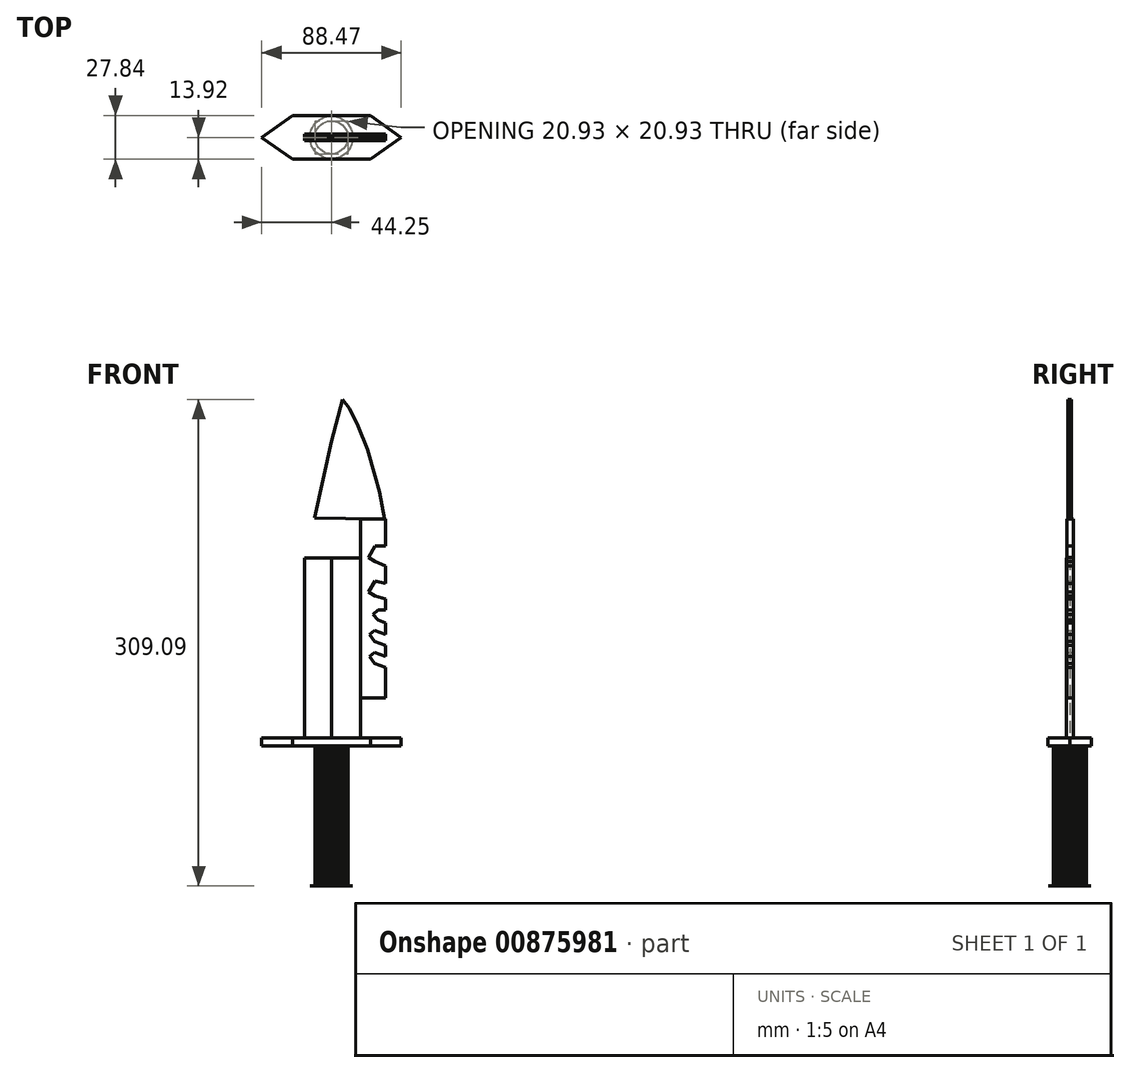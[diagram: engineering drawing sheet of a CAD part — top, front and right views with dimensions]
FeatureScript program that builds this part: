
annotation { "Feature Type Name" : "Feature", "Feature Type Description" : "" }
export const myFeature = defineFeature(function(context is Context, id is Id, definition is map)
    precondition{}
    {
        {
            var Q0;
            Q0=qCreatedBy(makeId("Top.planeOp"),FACE);
            var sketch = newSketch(context, id + "F0", { "sketchPlane" : qUnion([Q0])});
            skCircle(sketch, "E0.cCircle", {"center": v(0, 0) * mm, "radius": 13.55 * mm, "construction": true});
            skLineSegment(sketch, "E0.0", {"start": v(9, -10.17) * mm, "end": v(7.65, -11.22) * mm});
            skLineSegment(sketch, "E0.1", {"start": v(7.65, -11.22) * mm, "end": v(6.18, -12.09) * mm});
            skLineSegment(sketch, "E0.2", {"start": v(6.18, -12.09) * mm, "end": v(4.62, -12.77) * mm});
            skLineSegment(sketch, "E0.3", {"start": v(4.62, -12.77) * mm, "end": v(2.98, -13.25) * mm});
            skLineSegment(sketch, "E0.4", {"start": v(2.98, -13.25) * mm, "end": v(1.3, -13.51) * mm});
            skLineSegment(sketch, "E0.5", {"start": v(1.3, -13.51) * mm, "end": v(-0.4, -13.57) * mm});
            skLineSegment(sketch, "E0.6", {"start": v(-0.4, -13.57) * mm, "end": v(-2.1, -13.41) * mm});
            skLineSegment(sketch, "E0.7", {"start": v(-2.1, -13.41) * mm, "end": v(-3.77, -13.04) * mm});
            skLineSegment(sketch, "E0.8", {"start": v(-3.77, -13.04) * mm, "end": v(-5.38, -12.47) * mm});
            skLineSegment(sketch, "E0.9", {"start": v(-5.38, -12.47) * mm, "end": v(-6.9, -11.7) * mm});
            skLineSegment(sketch, "E0.10", {"start": v(-6.9, -11.7) * mm, "end": v(-8.3, -10.74) * mm});
            skLineSegment(sketch, "E0.11", {"start": v(-8.3, -10.74) * mm, "end": v(-9.59, -9.61) * mm});
            skLineSegment(sketch, "E0.12", {"start": v(-9.59, -9.61) * mm, "end": v(-10.72, -8.33) * mm});
            skLineSegment(sketch, "E0.13", {"start": v(-10.72, -8.33) * mm, "end": v(-11.68, -6.93) * mm});
            skLineSegment(sketch, "E0.14", {"start": v(-11.68, -6.93) * mm, "end": v(-12.45, -5.4) * mm});
            skLineSegment(sketch, "E0.15", {"start": v(-12.45, -5.4) * mm, "end": v(-13.03, -3.8) * mm});
            skLineSegment(sketch, "E0.16", {"start": v(-13.03, -3.8) * mm, "end": v(-13.4, -2.14) * mm});
            skLineSegment(sketch, "E0.17", {"start": v(-13.4, -2.14) * mm, "end": v(-13.57, -0.44) * mm});
            skLineSegment(sketch, "E0.18", {"start": v(-13.57, -0.44) * mm, "end": v(-13.52, 1.26) * mm});
            skLineSegment(sketch, "E0.19", {"start": v(-13.52, 1.26) * mm, "end": v(-13.25, 2.94) * mm});
            skLineSegment(sketch, "E0.20", {"start": v(-13.25, 2.94) * mm, "end": v(-12.78, 4.58) * mm});
            skLineSegment(sketch, "E0.21", {"start": v(-12.78, 4.58) * mm, "end": v(-12.1, 6.15) * mm});
            skLineSegment(sketch, "E0.22", {"start": v(-12.1, 6.15) * mm, "end": v(-11.24, 7.62) * mm});
            skLineSegment(sketch, "E0.23", {"start": v(-11.24, 7.62) * mm, "end": v(-10.2, 8.97) * mm});
            skLineSegment(sketch, "E0.24", {"start": v(-10.2, 8.97) * mm, "end": v(-9, 10.17) * mm});
            skLineSegment(sketch, "E0.25", {"start": v(-9, 10.17) * mm, "end": v(-7.65, 11.22) * mm});
            skLineSegment(sketch, "E0.26", {"start": v(-7.65, 11.22) * mm, "end": v(-6.18, 12.09) * mm});
            skLineSegment(sketch, "E0.27", {"start": v(-6.18, 12.09) * mm, "end": v(-4.62, 12.77) * mm});
            skLineSegment(sketch, "E0.28", {"start": v(-4.62, 12.77) * mm, "end": v(-2.98, 13.25) * mm});
            skLineSegment(sketch, "E0.29", {"start": v(-2.98, 13.25) * mm, "end": v(-1.3, 13.51) * mm});
            skLineSegment(sketch, "E0.30", {"start": v(-1.3, 13.51) * mm, "end": v(0.4, 13.57) * mm});
            skLineSegment(sketch, "E0.31", {"start": v(0.4, 13.57) * mm, "end": v(2.1, 13.41) * mm});
            skLineSegment(sketch, "E0.32", {"start": v(2.1, 13.41) * mm, "end": v(3.77, 13.04) * mm});
            skLineSegment(sketch, "E0.33", {"start": v(3.77, 13.04) * mm, "end": v(5.38, 12.47) * mm});
            skLineSegment(sketch, "E0.34", {"start": v(5.38, 12.47) * mm, "end": v(6.9, 11.7) * mm});
            skLineSegment(sketch, "E0.35", {"start": v(6.9, 11.7) * mm, "end": v(8.3, 10.74) * mm});
            skLineSegment(sketch, "E0.36", {"start": v(8.3, 10.74) * mm, "end": v(9.59, 9.61) * mm});
            skLineSegment(sketch, "E0.37", {"start": v(9.59, 9.61) * mm, "end": v(10.72, 8.33) * mm});
            skLineSegment(sketch, "E0.38", {"start": v(10.72, 8.33) * mm, "end": v(11.68, 6.93) * mm});
            skLineSegment(sketch, "E0.39", {"start": v(11.68, 6.93) * mm, "end": v(12.45, 5.4) * mm});
            skLineSegment(sketch, "E0.40", {"start": v(12.45, 5.4) * mm, "end": v(13.03, 3.8) * mm});
            skLineSegment(sketch, "E0.41", {"start": v(13.03, 3.8) * mm, "end": v(13.4, 2.14) * mm});
            skLineSegment(sketch, "E0.42", {"start": v(13.4, 2.14) * mm, "end": v(13.57, 0.44) * mm});
            skLineSegment(sketch, "E0.43", {"start": v(13.57, 0.44) * mm, "end": v(13.52, -1.26) * mm});
            skLineSegment(sketch, "E0.44", {"start": v(13.52, -1.26) * mm, "end": v(13.25, -2.94) * mm});
            skLineSegment(sketch, "E0.45", {"start": v(13.25, -2.94) * mm, "end": v(12.78, -4.58) * mm});
            skLineSegment(sketch, "E0.46", {"start": v(12.78, -4.58) * mm, "end": v(12.1, -6.15) * mm});
            skLineSegment(sketch, "E0.47", {"start": v(12.1, -6.15) * mm, "end": v(11.24, -7.62) * mm});
            skLineSegment(sketch, "E0.48", {"start": v(11.24, -7.62) * mm, "end": v(10.2, -8.97) * mm});
            skLineSegment(sketch, "E0.49", {"start": v(10.2, -8.97) * mm, "end": v(9, -10.17) * mm});
            skPoint(sketch, "E0.0.midPoint", {"position": v(8.32, -10.7) * mm});
            skSolve(sketch);
        }
        {
            var Q0;
            Q0 = qSketchRegion(id + "F0", true);
            extrude(context, id + "F1", {"entities" : qUnion([Q0]), "depth" : 1 / 50.8 * mm, "offsetDistance" : 25.4 * mm});
        }
        {
            var Q0;
            Q0=makeQuery(id+"F1.opExtrude","CAP_FACE",FACE,{"disambiguationData":[OSD([sQuery(id+"F0.wireOp",EDGE,"E0.0"),sQuery(id+"F0.wireOp",EDGE,"E0.1"),sQuery(id+"F0.wireOp",EDGE,"E0.2"),sQuery(id+"F0.wireOp",EDGE,"E0.3"),sQuery(id+"F0.wireOp",EDGE,"E0.4"),sQuery(id+"F0.wireOp",EDGE,"E0.5"),sQuery(id+"F0.wireOp",EDGE,"E0.6"),sQuery(id+"F0.wireOp",EDGE,"E0.7"),sQuery(id+"F0.wireOp",EDGE,"E0.8"),sQuery(id+"F0.wireOp",EDGE,"E0.9"),sQuery(id+"F0.wireOp",EDGE,"E0.10"),sQuery(id+"F0.wireOp",EDGE,"E0.11"),sQuery(id+"F0.wireOp",EDGE,"E0.12"),sQuery(id+"F0.wireOp",EDGE,"E0.13"),sQuery(id+"F0.wireOp",EDGE,"E0.14"),sQuery(id+"F0.wireOp",EDGE,"E0.15"),sQuery(id+"F0.wireOp",EDGE,"E0.16"),sQuery(id+"F0.wireOp",EDGE,"E0.17"),sQuery(id+"F0.wireOp",EDGE,"E0.18"),sQuery(id+"F0.wireOp",EDGE,"E0.19"),sQuery(id+"F0.wireOp",EDGE,"E0.20"),sQuery(id+"F0.wireOp",EDGE,"E0.21"),sQuery(id+"F0.wireOp",EDGE,"E0.22"),sQuery(id+"F0.wireOp",EDGE,"E0.23"),sQuery(id+"F0.wireOp",EDGE,"E0.24"),sQuery(id+"F0.wireOp",EDGE,"E0.25"),sQuery(id+"F0.wireOp",EDGE,"E0.26"),sQuery(id+"F0.wireOp",EDGE,"E0.27"),sQuery(id+"F0.wireOp",EDGE,"E0.28"),sQuery(id+"F0.wireOp",EDGE,"E0.29"),sQuery(id+"F0.wireOp",EDGE,"E0.30"),sQuery(id+"F0.wireOp",EDGE,"E0.31"),sQuery(id+"F0.wireOp",EDGE,"E0.32"),sQuery(id+"F0.wireOp",EDGE,"E0.33"),sQuery(id+"F0.wireOp",EDGE,"E0.34"),sQuery(id+"F0.wireOp",EDGE,"E0.35"),sQuery(id+"F0.wireOp",EDGE,"E0.36"),sQuery(id+"F0.wireOp",EDGE,"E0.37"),sQuery(id+"F0.wireOp",EDGE,"E0.38"),sQuery(id+"F0.wireOp",EDGE,"E0.39"),sQuery(id+"F0.wireOp",EDGE,"E0.40"),sQuery(id+"F0.wireOp",EDGE,"E0.41"),sQuery(id+"F0.wireOp",EDGE,"E0.42"),sQuery(id+"F0.wireOp",EDGE,"E0.43"),sQuery(id+"F0.wireOp",EDGE,"E0.44"),sQuery(id+"F0.wireOp",EDGE,"E0.45"),sQuery(id+"F0.wireOp",EDGE,"E0.46"),sQuery(id+"F0.wireOp",EDGE,"E0.47"),sQuery(id+"F0.wireOp",EDGE,"E0.48"),sQuery(id+"F0.wireOp",EDGE,"E0.49")])],"isStart":false});
            var sketch = newSketch(context, id + "F2", { "sketchPlane" : qUnion([Q0])});
            skCircle(sketch, "E1.cCircle", {"center": v(0, 0) * mm, "radius": 10.45 * mm, "construction": true});
            skLineSegment(sketch, "E1.0", {"start": v(3.77, -9.78) * mm, "end": v(2.2, -10.25) * mm});
            skLineSegment(sketch, "E1.1", {"start": v(2.2, -10.25) * mm, "end": v(0.56, -10.47) * mm});
            skLineSegment(sketch, "E1.2", {"start": v(0.56, -10.47) * mm, "end": v(-1.08, -10.42) * mm});
            skLineSegment(sketch, "E1.3", {"start": v(-1.08, -10.42) * mm, "end": v(-2.7, -10.13) * mm});
            skLineSegment(sketch, "E1.4", {"start": v(-2.7, -10.13) * mm, "end": v(-4.25, -9.58) * mm});
            skLineSegment(sketch, "E1.5", {"start": v(-4.25, -9.58) * mm, "end": v(-5.7, -8.8) * mm});
            skLineSegment(sketch, "E1.6", {"start": v(-5.7, -8.8) * mm, "end": v(-7, -7.8) * mm});
            skLineSegment(sketch, "E1.7", {"start": v(-7, -7.8) * mm, "end": v(-8.14, -6.6) * mm});
            skLineSegment(sketch, "E1.8", {"start": v(-8.14, -6.6) * mm, "end": v(-9.07, -5.25) * mm});
            skLineSegment(sketch, "E1.9", {"start": v(-9.07, -5.25) * mm, "end": v(-9.78, -3.77) * mm});
            skLineSegment(sketch, "E1.10", {"start": v(-9.78, -3.77) * mm, "end": v(-10.25, -2.2) * mm});
            skLineSegment(sketch, "E1.11", {"start": v(-10.25, -2.2) * mm, "end": v(-10.47, -0.56) * mm});
            skLineSegment(sketch, "E1.12", {"start": v(-10.47, -0.56) * mm, "end": v(-10.42, 1.08) * mm});
            skLineSegment(sketch, "E1.13", {"start": v(-10.42, 1.08) * mm, "end": v(-10.13, 2.7) * mm});
            skLineSegment(sketch, "E1.14", {"start": v(-10.13, 2.7) * mm, "end": v(-9.58, 4.25) * mm});
            skLineSegment(sketch, "E1.15", {"start": v(-9.58, 4.25) * mm, "end": v(-8.8, 5.7) * mm});
            skLineSegment(sketch, "E1.16", {"start": v(-8.8, 5.7) * mm, "end": v(-7.8, 7) * mm});
            skLineSegment(sketch, "E1.17", {"start": v(-7.8, 7) * mm, "end": v(-6.6, 8.14) * mm});
            skLineSegment(sketch, "E1.18", {"start": v(-6.6, 8.14) * mm, "end": v(-5.25, 9.07) * mm});
            skLineSegment(sketch, "E1.19", {"start": v(-5.25, 9.07) * mm, "end": v(-3.77, 9.78) * mm});
            skLineSegment(sketch, "E1.20", {"start": v(-3.77, 9.78) * mm, "end": v(-2.2, 10.25) * mm});
            skLineSegment(sketch, "E1.21", {"start": v(-2.2, 10.25) * mm, "end": v(-0.56, 10.47) * mm});
            skLineSegment(sketch, "E1.22", {"start": v(-0.56, 10.47) * mm, "end": v(1.08, 10.42) * mm});
            skLineSegment(sketch, "E1.23", {"start": v(1.08, 10.42) * mm, "end": v(2.7, 10.13) * mm});
            skLineSegment(sketch, "E1.24", {"start": v(2.7, 10.13) * mm, "end": v(4.25, 9.58) * mm});
            skLineSegment(sketch, "E1.25", {"start": v(4.25, 9.58) * mm, "end": v(5.7, 8.8) * mm});
            skLineSegment(sketch, "E1.26", {"start": v(5.7, 8.8) * mm, "end": v(7, 7.8) * mm});
            skLineSegment(sketch, "E1.27", {"start": v(7, 7.8) * mm, "end": v(8.14, 6.6) * mm});
            skLineSegment(sketch, "E1.28", {"start": v(8.14, 6.6) * mm, "end": v(9.07, 5.25) * mm});
            skLineSegment(sketch, "E1.29", {"start": v(9.07, 5.25) * mm, "end": v(9.78, 3.77) * mm});
            skLineSegment(sketch, "E1.30", {"start": v(9.78, 3.77) * mm, "end": v(10.25, 2.2) * mm});
            skLineSegment(sketch, "E1.31", {"start": v(10.25, 2.2) * mm, "end": v(10.47, 0.56) * mm});
            skLineSegment(sketch, "E1.32", {"start": v(10.47, 0.56) * mm, "end": v(10.42, -1.08) * mm});
            skLineSegment(sketch, "E1.33", {"start": v(10.42, -1.08) * mm, "end": v(10.13, -2.7) * mm});
            skLineSegment(sketch, "E1.34", {"start": v(10.13, -2.7) * mm, "end": v(9.58, -4.25) * mm});
            skLineSegment(sketch, "E1.35", {"start": v(9.58, -4.25) * mm, "end": v(8.8, -5.7) * mm});
            skLineSegment(sketch, "E1.36", {"start": v(8.8, -5.7) * mm, "end": v(7.8, -7) * mm});
            skLineSegment(sketch, "E1.37", {"start": v(7.8, -7) * mm, "end": v(6.6, -8.14) * mm});
            skLineSegment(sketch, "E1.38", {"start": v(6.6, -8.14) * mm, "end": v(5.25, -9.07) * mm});
            skLineSegment(sketch, "E1.39", {"start": v(5.25, -9.07) * mm, "end": v(3.77, -9.78) * mm});
            skPoint(sketch, "E1.0.midPoint", {"position": v(2.98, -10.02) * mm});
            skSolve(sketch);
        }
        {
            var Q0;
            Q0 = qSketchRegion(id + "F2", true);
            extrude(context, id + "F3", {"entities" : qUnion([Q0]), "operationType" : NewBodyOperationType.ADD, "depth" : 88.9 * mm, "offsetDistance" : 25.4 * mm});
        }
        {
            var Q0;
            Q0=makeQuery(id+"F3.opExtrude","CAP_FACE",FACE,{"disambiguationData":[OSD([sQuery(id+"F2.wireOp",EDGE,"E1.0"),sQuery(id+"F2.wireOp",EDGE,"E1.1"),sQuery(id+"F2.wireOp",EDGE,"E1.2"),sQuery(id+"F2.wireOp",EDGE,"E1.3"),sQuery(id+"F2.wireOp",EDGE,"E1.4"),sQuery(id+"F2.wireOp",EDGE,"E1.5"),sQuery(id+"F2.wireOp",EDGE,"E1.6"),sQuery(id+"F2.wireOp",EDGE,"E1.7"),sQuery(id+"F2.wireOp",EDGE,"E1.8"),sQuery(id+"F2.wireOp",EDGE,"E1.9"),sQuery(id+"F2.wireOp",EDGE,"E1.10"),sQuery(id+"F2.wireOp",EDGE,"E1.11"),sQuery(id+"F2.wireOp",EDGE,"E1.12"),sQuery(id+"F2.wireOp",EDGE,"E1.13"),sQuery(id+"F2.wireOp",EDGE,"E1.14"),sQuery(id+"F2.wireOp",EDGE,"E1.15"),sQuery(id+"F2.wireOp",EDGE,"E1.16"),sQuery(id+"F2.wireOp",EDGE,"E1.17"),sQuery(id+"F2.wireOp",EDGE,"E1.18"),sQuery(id+"F2.wireOp",EDGE,"E1.19"),sQuery(id+"F2.wireOp",EDGE,"E1.20"),sQuery(id+"F2.wireOp",EDGE,"E1.21"),sQuery(id+"F2.wireOp",EDGE,"E1.22"),sQuery(id+"F2.wireOp",EDGE,"E1.23"),sQuery(id+"F2.wireOp",EDGE,"E1.24"),sQuery(id+"F2.wireOp",EDGE,"E1.25"),sQuery(id+"F2.wireOp",EDGE,"E1.26"),sQuery(id+"F2.wireOp",EDGE,"E1.27"),sQuery(id+"F2.wireOp",EDGE,"E1.28"),sQuery(id+"F2.wireOp",EDGE,"E1.29"),sQuery(id+"F2.wireOp",EDGE,"E1.30"),sQuery(id+"F2.wireOp",EDGE,"E1.31"),sQuery(id+"F2.wireOp",EDGE,"E1.32"),sQuery(id+"F2.wireOp",EDGE,"E1.33"),sQuery(id+"F2.wireOp",EDGE,"E1.34"),sQuery(id+"F2.wireOp",EDGE,"E1.35"),sQuery(id+"F2.wireOp",EDGE,"E1.36"),sQuery(id+"F2.wireOp",EDGE,"E1.37"),sQuery(id+"F2.wireOp",EDGE,"E1.38"),sQuery(id+"F2.wireOp",EDGE,"E1.39")])],"isStart":false});
            var sketch = newSketch(context, id + "F4", { "sketchPlane" : qUnion([Q0])});
            skLineSegment(sketch, "E2.bottom", {"start": v(24.8, -13.92) * mm, "end": v(-24.8, -13.92) * mm});
            skLineSegment(sketch, "E2.top", {"start": v(24.8, 13.92) * mm, "end": v(-24.8, 13.92) * mm});
            skLineSegment(sketch, "E2.left", {"start": v(24.8, -13.92) * mm, "end": v(24.8, 13.92) * mm});
            skLineSegment(sketch, "E2.right", {"start": v(-24.8, -13.92) * mm, "end": v(-24.8, 13.92) * mm});
            skPoint(sketch, "E2.middle", {"position": v(0, 0) * mm});
            skSolve(sketch);
        }
        {
            var Q0;
            Q0 = qSketchRegion(id + "F4", true);
            extrude(context, id + "F5", {"entities" : qUnion([Q0]), "operationType" : NewBodyOperationType.ADD, "depth" : 5.08 * mm, "offsetDistance" : 25.4 * mm});
        }
        {
            var Q0;
            Q0=makeQuery(id+"F5.opExtrude","CAP_FACE",FACE,{"disambiguationData":[OSD([sQuery(id+"F4.wireOp",EDGE,"E2.bottom"),sQuery(id+"F4.wireOp",EDGE,"E2.top"),sQuery(id+"F4.wireOp",EDGE,"E2.left"),sQuery(id+"F4.wireOp",EDGE,"E2.right")])],"isStart":true});
            var sketch = newSketch(context, id + "F6", { "sketchPlane" : qUnion([Q0])});
            skLineSegment(sketch, "E3", {"start": v(-24.8, -13.92) * mm, "end": v(-44.25, 0) * mm});
            skLineSegment(sketch, "E4", {"start": v(-44.25, 0) * mm, "end": v(-24.8, 13.92) * mm});
            skLineSegment(sketch, "E5", {"start": v(24.8, 13.92) * mm, "end": v(44.22, 0) * mm});
            skLineSegment(sketch, "E6", {"start": v(44.22, 0) * mm, "end": v(24.8, -13.92) * mm});
            skSolve(sketch);
        }
        {
            var Q0;
            Q0=makeQuery(id+"F6.imprint","IMPRINT",FACE,{"disambiguationData":[TD([[makeQuery(id+"F6.imprint","IMPRINT",EDGE,{"derivedFrom":sQuery(id+"F6.wireOp",EDGE,"E3")}),-1.0]])]});
            extrude(context, id + "F7", {"entities" : qUnion([Q0]), "operationType" : NewBodyOperationType.ADD, "oppositeDirection" : true, "depth" : 5.08 * mm, "offsetDistance" : 25.4 * mm});
        }
        {
            var Q0;
            Q0=makeQuery(id+"F6.imprint","IMPRINT",FACE,{"disambiguationData":[TD([[makeQuery(id+"F6.imprint","IMPRINT",EDGE,{"derivedFrom":sQuery(id+"F6.wireOp",EDGE,"E5")}),-1.0]])]});
            extrude(context, id + "F8", {"entities" : qUnion([Q0]), "operationType" : NewBodyOperationType.ADD, "oppositeDirection" : true, "depth" : 5.08 * mm, "offsetDistance" : 25.4 * mm});
        }
        {
            var Q0;
            {var subQ0=sQuery(id+"F4.wireOp",EDGE,"E2.left");var subQ1=sQuery(id+"F4.wireOp",EDGE,"E2.right");Q0=makeQuery(id+"F8.boolean.opBoolean","MERGE",FACE,{"derivedFrom":[makeQuery(id+"F7.boolean.opBoolean","MERGE",FACE,{"derivedFrom":[makeQuery(id+"F5.opExtrude","CAP_FACE",FACE,{"disambiguationData":[OSD([sQuery(id+"F4.wireOp",EDGE,"E2.bottom"),sQuery(id+"F4.wireOp",EDGE,"E2.top"),subQ0,subQ1])],"isStart":false}),makeQuery(id+"F7.opExtrude","CAP_FACE",FACE,{"disambiguationData":[OSD([subQ1,sQuery(id+"F6.wireOp",EDGE,"E3"),sQuery(id+"F6.wireOp",EDGE,"E4")])],"isStart":false})]}),makeQuery(id+"F8.opExtrude","CAP_FACE",FACE,{"disambiguationData":[OSD([subQ0,sQuery(id+"F6.wireOp",EDGE,"E5"),sQuery(id+"F6.wireOp",EDGE,"E6")])],"isStart":false})]});}
            var sketch = newSketch(context, id + "F9", { "sketchPlane" : qUnion([Q0])});
            skPoint(sketch, "E7.firstSnap0", {"position": v(34.5, 6.96) * mm});
            skLineSegment(sketch, "E7.bottom", {"start": v(34.5, 2.26) * mm, "end": v(-17.1, 2.26) * mm});
            skLineSegment(sketch, "E7.top", {"start": v(34.5, -2.17) * mm, "end": v(-17.1, -2.17) * mm});
            skLineSegment(sketch, "E7.left", {"start": v(34.5, 2.26) * mm, "end": v(34.5, -2.17) * mm});
            skLineSegment(sketch, "E7.right", {"start": v(-17.1, 2.26) * mm, "end": v(-17.1, -2.17) * mm});
            skSolve(sketch);
        }
        {
            var Q0;
            Q0 = qSketchRegion(id + "F9", true);
            extrude(context, id + "F10", {"entities" : qUnion([Q0]), "operationType" : NewBodyOperationType.ADD, "depth" : 1 / 50.8 * mm, "offsetDistance" : 25.4 * mm});
        }
        {
            var Q0;
            Q0=makeQuery(id+"F10.opExtrude","CAP_FACE",FACE,{"disambiguationData":[OSD([sQuery(id+"F9.wireOp",EDGE,"E7.bottom"),sQuery(id+"F9.wireOp",EDGE,"E7.top"),sQuery(id+"F9.wireOp",EDGE,"E7.left"),sQuery(id+"F9.wireOp",EDGE,"E7.right")])],"isStart":false});
            var sketch = newSketch(context, id + "F11", { "sketchPlane" : qUnion([Q0])});
            skLineSegment(sketch, "E8.bottom", {"start": v(0, 2.26) * mm, "end": v(18.53, 2.26) * mm});
            skLineSegment(sketch, "E8.top", {"start": v(0, -2.17) * mm, "end": v(18.53, -2.17) * mm});
            skLineSegment(sketch, "E8.left", {"start": v(0, 2.26) * mm, "end": v(0, -2.17) * mm});
            skLineSegment(sketch, "E8.right", {"start": v(18.53, 2.26) * mm, "end": v(18.53, -2.17) * mm});
            skSolve(sketch);
        }
        {
            var Q0;
            Q0 = qSketchRegion(id + "F11", true);
            extrude(context, id + "F12", {"entities" : qUnion([Q0]), "operationType" : NewBodyOperationType.ADD, "depth" : 114.3 * mm, "offsetDistance" : 25.4 * mm});
        }
        {
            var Q0;
            {var subQ0=sQuery(id+"F9.wireOp",EDGE,"E7.right");var subQ1=sQuery(id+"F9.wireOp",EDGE,"E7.top");var subQ2=sQuery(id+"F9.wireOp",EDGE,"E7.bottom");Q0=makeQuery(id+"F12.boolean.opBoolean","SPLIT",FACE,{"disambiguationData":[TD([makeQuery(id+"F10.opExtrude","SWEPT_FACE",FACE,{"disambiguationData":[OSD([subQ0])]})])],"derivedFrom":makeQuery(id+"F10.opExtrude","CAP_FACE",FACE,{"disambiguationData":[OSD([subQ2,subQ1,sQuery(id+"F9.wireOp",EDGE,"E7.left"),subQ0])],"isStart":false})});}
            var sketch = newSketch(context, id + "F13", { "sketchPlane" : qUnion([Q0])});
            skLineSegment(sketch, "E9", {"start": v(0, 2.26) * mm, "end": v(-17.1, 0) * mm});
            skLineSegment(sketch, "E10", {"start": v(-17.1, 0) * mm, "end": v(0, -2.17) * mm});
            skLineSegment(sketch, "E11", {"start": v(0, -2.17) * mm, "end": v(0, 2.26) * mm});
            skSolve(sketch);
        }
        {
            var Q0;
            Q0=makeQuery(id+"F13.imprint","IMPRINT",FACE,{"disambiguationData":[TD([[makeQuery(id+"F13.imprint","IMPRINT",EDGE,{"derivedFrom":sQuery(id+"F13.wireOp",EDGE,"E9")}),1.0]])]});
            extrude(context, id + "F14", {"entities" : qUnion([Q0]), "operationType" : NewBodyOperationType.ADD, "depth" : 114.3 * mm, "offsetDistance" : 25.4 * mm});
        }
        {
            var Q0;
            Q0=makeQuery(id+"F12.boolean.opBoolean","MERGE",FACE,{"derivedFrom":[makeQuery(id+"F10.opExtrude","SWEPT_FACE",FACE,{"disambiguationData":[OSD([sQuery(id+"F9.wireOp",EDGE,"E7.bottom")])]}),makeQuery(id+"F12.opExtrude","SWEPT_FACE",FACE,{"disambiguationData":[OSD([sQuery(id+"F11.wireOp",EDGE,"E8.bottom")])]})]});
            var sketch = newSketch(context, id + "F15", { "sketchPlane" : qUnion([Q0])});
            skLineSegment(sketch, "E12", {"start": v(-34.5, 119.38) * mm, "end": v(-34.5, 124.43) * mm});
            skLineSegment(sketch, "E13", {"start": v(-34.5, 124.43) * mm, "end": v(-23.3, 126.84) * mm});
            skLineSegment(sketch, "E14", {"start": v(-23.26, 126.61) * mm, "end": v(-19.36, 131.77) * mm});
            skLineSegment(sketch, "E15", {"start": v(-19.36, 131.77) * mm, "end": v(-23.41, 134.83) * mm});
            skLineSegment(sketch, "E16", {"start": v(-23.41, 134.83) * mm, "end": v(-34.5, 131.77) * mm});
            skLineSegment(sketch, "E17", {"start": v(-34.5, 131.77) * mm, "end": v(-34.5, 138.87) * mm});
            skLineSegment(sketch, "E18", {"start": v(-34.5, 138.87) * mm, "end": v(-27.46, 141.44) * mm});
            skLineSegment(sketch, "E19", {"start": v(-27.46, 141.44) * mm, "end": v(-24.07, 145.92) * mm});
            skLineSegment(sketch, "E20", {"start": v(-24.07, 145.92) * mm, "end": v(-27.46, 148.49) * mm});
            skLineSegment(sketch, "E21", {"start": v(-27.46, 148.49) * mm, "end": v(-34.5, 145.92) * mm});
            skLineSegment(sketch, "E22", {"start": v(-34.5, 145.92) * mm, "end": v(-34.5, 152.68) * mm});
            skLineSegment(sketch, "E23", {"start": v(-34.5, 152.68) * mm, "end": v(-27.46, 155.25) * mm});
            skLineSegment(sketch, "E24", {"start": v(-27.46, 155.25) * mm, "end": v(-24.07, 159.74) * mm});
            skLineSegment(sketch, "E25", {"start": v(-24.07, 159.74) * mm, "end": v(-27.46, 162.3) * mm});
            skLineSegment(sketch, "E26", {"start": v(-27.46, 162.3) * mm, "end": v(-34.5, 159.74) * mm});
            skLineSegment(sketch, "E27", {"start": v(-34.5, 159.74) * mm, "end": v(-34.5, 167.06) * mm});
            skLineSegment(sketch, "E28", {"start": v(-34.5, 167.06) * mm, "end": v(-29.64, 169.14) * mm});
            skLineSegment(sketch, "E29", {"start": v(-29.64, 169.14) * mm, "end": v(-26.5, 172.52) * mm});
            skLineSegment(sketch, "E30", {"start": v(-26.5, 172.52) * mm, "end": v(-29.64, 175.42) * mm});
            skLineSegment(sketch, "E31", {"start": v(-29.64, 175.42) * mm, "end": v(-34.5, 175.42) * mm});
            skLineSegment(sketch, "E32", {"start": v(-34.5, 175.42) * mm, "end": v(-34.5, 182.4) * mm});
            skLineSegment(sketch, "E33", {"start": v(-34.5, 182.4) * mm, "end": v(-27.86, 184.14) * mm});
            skLineSegment(sketch, "E34", {"start": v(-27.86, 184.14) * mm, "end": v(-23.5, 186.9) * mm});
            skLineSegment(sketch, "E35", {"start": v(-23.5, 186.9) * mm, "end": v(-27.86, 193.8) * mm});
            skLineSegment(sketch, "E36", {"start": v(-27.86, 193.8) * mm, "end": v(-34.5, 192.31) * mm});
            skLineSegment(sketch, "E37", {"start": v(-34.5, 192.31) * mm, "end": v(-34.5, 203.43) * mm});
            skLineSegment(sketch, "E38", {"start": v(-34.5, 203.43) * mm, "end": v(-27.86, 206.05) * mm});
            skLineSegment(sketch, "E39", {"start": v(-27.86, 206.05) * mm, "end": v(-23.5, 208.63) * mm});
            skLineSegment(sketch, "E40", {"start": v(-23.5, 208.63) * mm, "end": v(-27.86, 216.03) * mm});
            skLineSegment(sketch, "E41", {"start": v(-27.86, 216.03) * mm, "end": v(-34.5, 216.03) * mm});
            skLineSegment(sketch, "E42", {"start": v(-34.5, 216.03) * mm, "end": v(-34.5, 233.07) * mm});
            skLineSegment(sketch, "E43", {"start": v(-34.5, 233.07) * mm, "end": v(-18.53, 233.07) * mm});
            skLineSegment(sketch, "E44", {"start": v(-18.53, 233.07) * mm, "end": v(-18.53, 119.38) * mm});
            skLineSegment(sketch, "E45", {"start": v(-18.53, 119.38) * mm, "end": v(-34.5, 119.38) * mm});
            skLineSegment(sketch, "E46.top", {"start": v(-18.53, 233.07) * mm, "end": v(-34.5, 233.07) * mm});
            skLineSegment(sketch, "E46.left", {"start": v(-18.53, 119.38) * mm, "end": v(-18.53, 233.07) * mm});
            skLineSegment(sketch, "E46.right", {"start": v(-34.5, 119.38) * mm, "end": v(-34.5, 233.07) * mm});
            skSolve(sketch);
        }
        {
            var Q0;
            {var subQ8=sQuery(id+"F15.wireOp",EDGE,"E19");Q0=makeQuery(id+"F15.imprint","IMPRINT",FACE,{"disambiguationData":[TD([[makeQuery(id+"F15.imprint","IMPRINT",EDGE,{"derivedFrom":subQ8}),-1.0]])]});}
            extrude(context, id + "F16", {"entities" : qUnion([Q0]), "operationType" : NewBodyOperationType.ADD, "oppositeDirection" : true, "depth" : 4.06 * mm, "offsetDistance" : 25.4 * mm});
        }
        {
            var Q0;
            Q0=qCreatedBy(makeId("Front.planeOp"),FACE);
            var sketch = newSketch(context, id + "F17", { "sketchPlane" : qUnion([Q0])});
            skLineSegment(sketch, "E47", {"start": v(33.72, 233) * mm, "end": v(30.61, 250.21) * mm});
            skLineSegment(sketch, "E48", {"start": v(30.61, 250.21) * mm, "end": v(27.63, 260.38) * mm});
            skLineSegment(sketch, "E49", {"start": v(27.63, 260.38) * mm, "end": v(23.05, 277.19) * mm});
            skLineSegment(sketch, "E50", {"start": v(23.05, 277.19) * mm, "end": v(16.9, 292.23) * mm});
            skLineSegment(sketch, "E51", {"start": v(16.9, 292.23) * mm, "end": v(11.68, 303.23) * mm});
            skLineSegment(sketch, "E52", {"start": v(11.68, 303.23) * mm, "end": v(7.18, 309.1) * mm});
            skLineSegment(sketch, "E53", {"start": v(7.18, 309.1) * mm, "end": v(0, 282.52) * mm});
            skLineSegment(sketch, "E54", {"start": v(0, 282.52) * mm, "end": v(-10.86, 233.66) * mm});
            skLineSegment(sketch, "E55", {"start": v(-10.86, 233.66) * mm, "end": v(33.72, 233) * mm});
            skSolve(sketch);
        }
        {
            var Q0;
            Q0=makeQuery(id+"F17.imprint","IMPRINT",FACE,{"disambiguationData":[TD([[makeQuery(id+"F17.imprint","IMPRINT",EDGE,{"derivedFrom":sQuery(id+"F17.wireOp",EDGE,"E47")}),1.0]])]});
            extrude(context, id + "F18", {"entities" : qUnion([Q0]), "operationType" : NewBodyOperationType.ADD, "depth" : 1.02 * mm, "offsetDistance" : 25.4 * mm});
        }
        {
            var Q0;
            Q0 = qSketchRegion(id + "F17", true);
            extrude(context, id + "F19", {"entities" : qUnion([Q0]), "operationType" : NewBodyOperationType.ADD, "oppositeDirection" : true, "depth" : 1.02 * mm, "offsetDistance" : 25.4 * mm});
        }
    });
